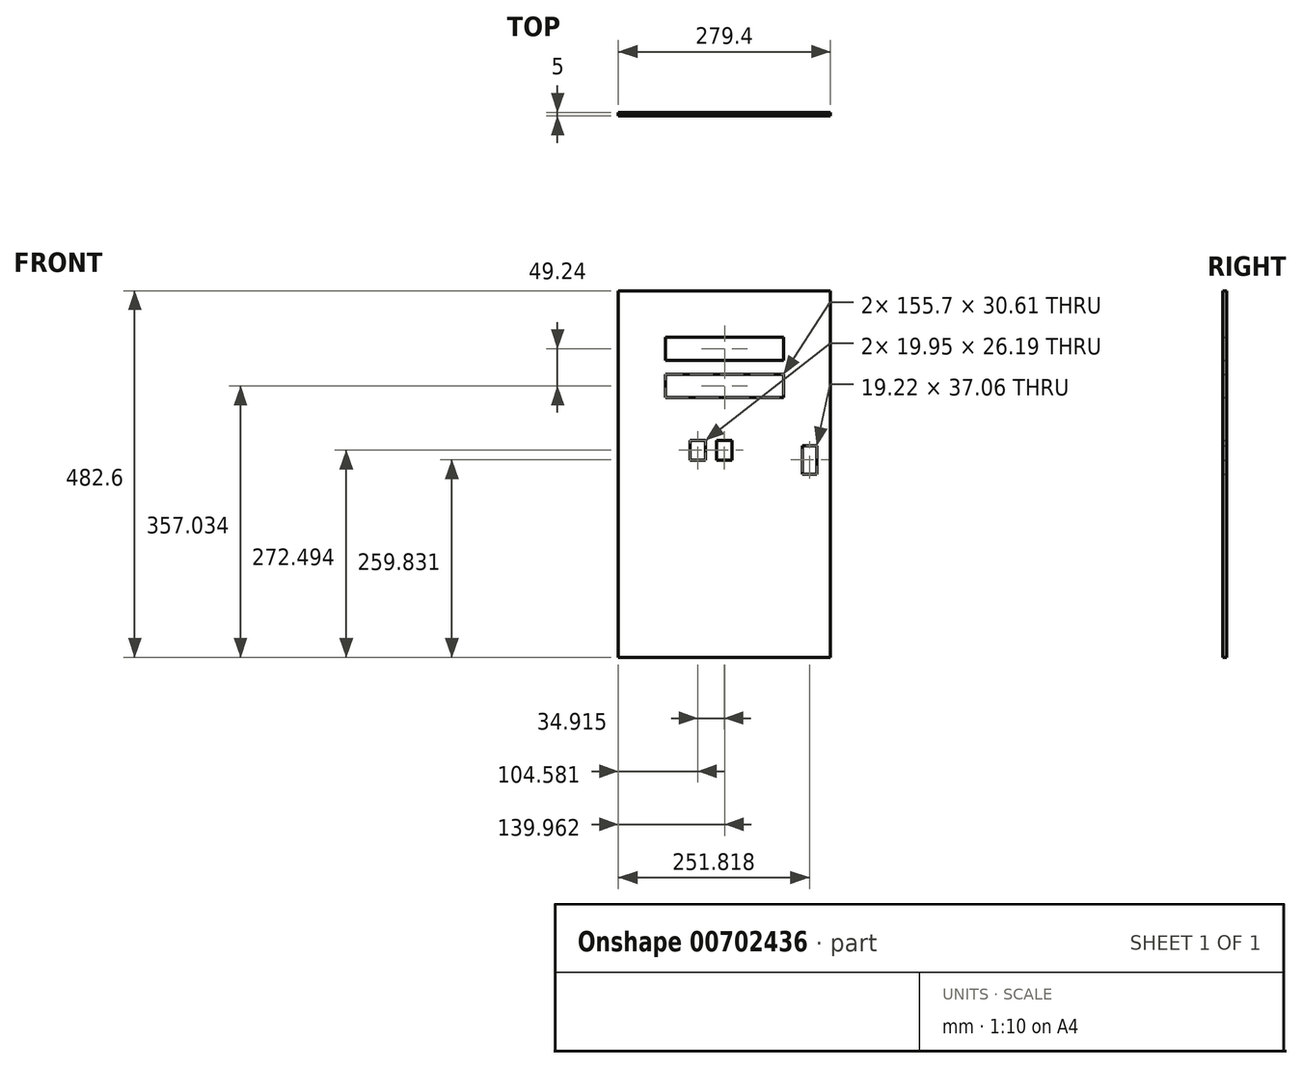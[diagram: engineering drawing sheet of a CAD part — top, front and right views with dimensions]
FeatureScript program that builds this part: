
annotation { "Feature Type Name" : "Feature", "Feature Type Description" : "" }
export const myFeature = defineFeature(function(context is Context, id is Id, definition is map)
    precondition{}
    {
        {
            var Q0;
            Q0=qCreatedBy(makeId("Front.planeOp"),FACE);
            var sketch = newSketch(context, id + "F0", { "sketchPlane" : qUnion([Q0])});
            skLineSegment(sketch, "E0.bottom", {"start": v(-139.7, 241.3) * mm, "end": v(139.7, 241.3) * mm});
            skLineSegment(sketch, "E0.top", {"start": v(-139.7, -241.3) * mm, "end": v(139.7, -241.3) * mm});
            skLineSegment(sketch, "E0.left", {"start": v(-139.7, 241.3) * mm, "end": v(-139.7, -241.3) * mm});
            skLineSegment(sketch, "E0.right", {"start": v(139.7, 241.3) * mm, "end": v(139.7, -241.3) * mm});
            skPoint(sketch, "E0.middle", {"position": v(0, 0) * mm});
            skLineSegment(sketch, "E1.bottom", {"start": v(-77.6, 180.28) * mm, "end": v(78.11, 180.28) * mm});
            skLineSegment(sketch, "E1.top", {"start": v(-77.6, 149.67) * mm, "end": v(78.11, 149.67) * mm});
            skLineSegment(sketch, "E1.left", {"start": v(-77.6, 180.28) * mm, "end": v(-77.6, 149.67) * mm});
            skLineSegment(sketch, "E1.right", {"start": v(78.11, 180.28) * mm, "end": v(78.11, 149.67) * mm});
            skLineSegment(sketch, "E2.bottom", {"start": v(78.11, 131.04) * mm, "end": v(-77.6, 131.04) * mm});
            skLineSegment(sketch, "E2.top", {"start": v(78.11, 100.43) * mm, "end": v(-77.6, 100.43) * mm});
            skLineSegment(sketch, "E2.left", {"start": v(78.11, 131.04) * mm, "end": v(78.11, 100.43) * mm});
            skLineSegment(sketch, "E2.right", {"start": v(-77.6, 131.04) * mm, "end": v(-77.6, 100.43) * mm});
            skLineSegment(sketch, "E3.bottom", {"start": v(121.73, 37.06) * mm, "end": v(102.5, 37.06) * mm});
            skLineSegment(sketch, "E3.top", {"start": v(121.73, 0) * mm, "end": v(102.5, 0) * mm});
            skLineSegment(sketch, "E3.left", {"start": v(121.73, 37.06) * mm, "end": v(121.73, 0) * mm});
            skLineSegment(sketch, "E3.right", {"start": v(102.5, 37.06) * mm, "end": v(102.5, 0) * mm});
            skLineSegment(sketch, "E4.bottom", {"start": v(-45.1, 44.29) * mm, "end": v(-25.14, 44.29) * mm});
            skLineSegment(sketch, "E4.top", {"start": v(-45.1, 18.1) * mm, "end": v(-25.14, 18.1) * mm});
            skLineSegment(sketch, "E4.left", {"start": v(-45.1, 44.29) * mm, "end": v(-45.1, 18.1) * mm});
            skLineSegment(sketch, "E4.right", {"start": v(-25.14, 44.29) * mm, "end": v(-25.14, 18.1) * mm});
            skLineSegment(sketch, "E5.bottom", {"start": v(-10.18, 44.29) * mm, "end": v(9.77, 44.29) * mm});
            skLineSegment(sketch, "E5.top", {"start": v(-10.18, 18.1) * mm, "end": v(9.77, 18.1) * mm});
            skLineSegment(sketch, "E5.left", {"start": v(-10.18, 44.29) * mm, "end": v(-10.18, 18.1) * mm});
            skLineSegment(sketch, "E5.right", {"start": v(9.77, 44.29) * mm, "end": v(9.77, 18.1) * mm});
            skSolve(sketch);
        }
        {
            var Q0;
            Q0 = qSketchRegion(id + "F0", true);
            extrude(context, id + "F1", {"entities" : qUnion([Q0]), "depth" : 5 * mm, "offsetDistance" : 25.4 * mm});
        }
    });
